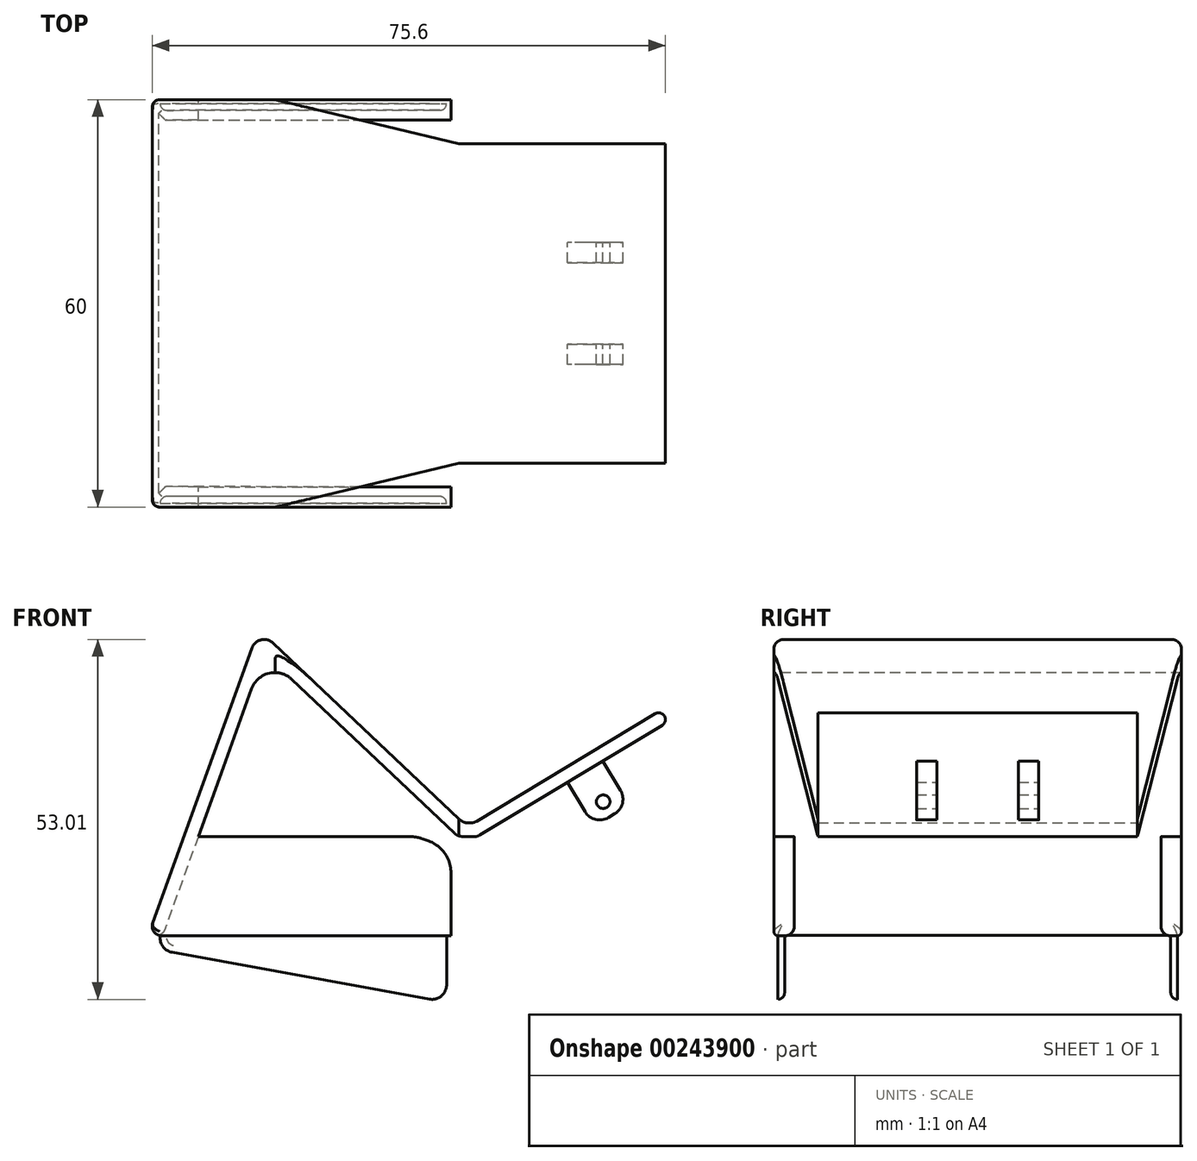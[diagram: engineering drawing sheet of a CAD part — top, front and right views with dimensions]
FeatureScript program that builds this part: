
annotation { "Feature Type Name" : "Feature", "Feature Type Description" : "" }
export const myFeature = defineFeature(function(context is Context, id is Id, definition is map)
    precondition{}
    {
        {
            var Q0;
            Q0=qCreatedBy(makeId("Front.planeOp"),FACE);
            var sketch = newSketch(context, id + "F0", { "sketchPlane" : qUnion([Q0])});
            skPoint(sketch, "E0.middle", {"position": v(-5, 4.31) * mm});
            skLineSegment(sketch, "E1", {"start": v(-52, -14.64) * mm, "end": v(-35.7, 30.54) * mm});
            skLineSegment(sketch, "E2", {"start": v(-35.7, 30.54) * mm, "end": v(-5.57, 2.03) * mm});
            skLineSegment(sketch, "E3", {"start": v(-4.04, 2) * mm, "end": v(-5.57, 2.03) * mm});
            skLineSegment(sketch, "E4", {"start": v(-4.04, 2) * mm, "end": v(23.56, 18.63) * mm});
            skLineSegment(sketch, "E5.0", {"start": v(-3.5, 0) * mm, "end": v(24.59, 16.91) * mm});
            skLineSegment(sketch, "E5.1", {"start": v(-3.5, 0) * mm, "end": v(-6.38, 0.04) * mm});
            skLineSegment(sketch, "E5.2", {"start": v(-34.85, 26.99) * mm, "end": v(-6.38, 0.04) * mm});
            skLineSegment(sketch, "E5.3", {"start": v(-49.86, -14.62) * mm, "end": v(-34.85, 26.99) * mm});
            skLineSegment(sketch, "E6", {"start": v(-49.86, -14.62) * mm, "end": v(-52, -14.64) * mm});
            skLineSegment(sketch, "E7", {"start": v(23.56, 18.63) * mm, "end": v(24.59, 16.91) * mm});
            skSolve(sketch);
        }
        {
            var Q0;
            Q0=makeQuery(id+"F0.imprint","IMPRINT",FACE,{"disambiguationData":[TD([[makeQuery(id+"F0.imprint","IMPRINT",EDGE,{"derivedFrom":sQuery(id+"F0.wireOp",EDGE,"E1")}),-1.0]])]});
            extrude(context, id + "F1", {"entities" : qUnion([Q0]), "endBound" : BoundingType.SYMMETRIC, "depth" : 60 * mm});
        }
        {
            var Q0;
            Q0=makeQuery(id+"F1.opExtrude","SWEPT_EDGE",EDGE,{"disambiguationData":[OSD([sQuery(id+"F0.wireOp",EDGE,"E1"),sQuery(id+"F0.wireOp",EDGE,"E2")])]});
            fillet(context, id + "F2", {"entities" : qUnion([Q0]), "radius" : 1.94 * mm, "tangentPropagation" : true, "allowEdgeOverflow" : false});
        }
        {
            var Q0;
            Q0=makeQuery(id+"F1.opExtrude","SWEPT_EDGE",EDGE,{"disambiguationData":[OSD([sQuery(id+"F0.wireOp",EDGE,"E5.2"),sQuery(id+"F0.wireOp",EDGE,"E5.3")])]});
            fillet(context, id + "F3", {"entities" : qUnion([Q0]), "radius" : 3.63 * mm, "tangentPropagation" : true, "allowEdgeOverflow" : false});
        }
        {
            var Q0;
            Q0=makeQuery(id+"F1.opExtrude","SWEPT_EDGE",EDGE,{"disambiguationData":[OSD([sQuery(id+"F0.wireOp",EDGE,"E5.1"),sQuery(id+"F0.wireOp",EDGE,"E5.2")])]});
            var Q1;
            Q1=makeQuery(id+"F1.opExtrude","SWEPT_EDGE",EDGE,{"disambiguationData":[OSD([sQuery(id+"F0.wireOp",EDGE,"E5.0"),sQuery(id+"F0.wireOp",EDGE,"E5.1")])]});
            var Q2;
            Q2=makeQuery(id+"F1.opExtrude","SWEPT_EDGE",EDGE,{"disambiguationData":[OSD([sQuery(id+"F0.wireOp",EDGE,"E2"),sQuery(id+"F0.wireOp",EDGE,"E3")])]});
            var Q3;
            Q3=makeQuery(id+"F1.opExtrude","SWEPT_EDGE",EDGE,{"disambiguationData":[OSD([sQuery(id+"F0.wireOp",EDGE,"E3"),sQuery(id+"F0.wireOp",EDGE,"E4")])]});
            fillet(context, id + "F4", {"entities" : qUnion([Q0, Q1, Q2, Q3]), "radius" : 1.68 * mm, "allowEdgeOverflow" : false});
        }
        {
            var Q0;
            Q0=makeQuery(id+"F1.opExtrude","SWEPT_FACE",FACE,{"disambiguationData":[OSD([sQuery(id+"F0.wireOp",EDGE,"E5.0")])]});
            var sketch = newSketch(context, id + "F5", { "sketchPlane" : qUnion([Q0])});
            skLineSegment(sketch, "E8.bottom", {"start": v(18.6, 9) * mm, "end": v(12.5, 9) * mm});
            skLineSegment(sketch, "E8.top", {"start": v(18.6, -9) * mm, "end": v(12.5, -9) * mm});
            skLineSegment(sketch, "E8.left", {"start": v(18.6, 9) * mm, "end": v(18.6, -9) * mm});
            skLineSegment(sketch, "E8.right", {"start": v(12.5, 9) * mm, "end": v(12.5, -9) * mm});
            skPoint(sketch, "E8.middle", {"position": v(15.55, 0) * mm});
            skSolve(sketch);
        }
        {
            var Q0;
            Q0=makeQuery(id+"F5.imprint","IMPRINT",FACE,{"disambiguationData":[TD([[makeQuery(id+"F5.imprint","IMPRINT",EDGE,{"derivedFrom":sQuery(id+"F5.wireOp",EDGE,"E8.bottom")}),1.0]])]});
            extrude(context, id + "F6", {"entities" : qUnion([Q0]), "operationType" : NewBodyOperationType.ADD, "depth" : 7.56 * mm});
        }
        {
            var Q0;
            Q0=qCreatedBy(makeId("Front.planeOp"),FACE);
            var sketch = newSketch(context, id + "F7", { "sketchPlane" : qUnion([Q0])});
            skCircle(sketch, "E9", {"center": v(15.05, 5.15) * mm, "radius": 1 * mm});
            skSolve(sketch);
        }
        {
            var Q0;
            Q0 = qSketchRegion(id + "F7", true);
            extrude(context, id + "F8", {"entities" : qUnion([Q0]), "operationType" : NewBodyOperationType.REMOVE, "endBound" : BoundingType.SYMMETRIC, "depth" : 25 * mm});
        }
        {
            var Q0;
            Q0=makeQuery(id+"F1.opExtrude","SWEPT_EDGE",EDGE,{"disambiguationData":[OSD([sQuery(id+"F0.wireOp",EDGE,"E4"),sQuery(id+"F0.wireOp",EDGE,"E7")])]});
            var Q1;
            Q1=makeQuery(id+"F1.opExtrude","SWEPT_EDGE",EDGE,{"disambiguationData":[OSD([sQuery(id+"F0.wireOp",EDGE,"E5.0"),sQuery(id+"F0.wireOp",EDGE,"E7")])]});
            fillet(context, id + "F9", {"entities" : qUnion([Q0, Q1]), "radius" : 1 * mm, "tangentPropagation" : true, "allowEdgeOverflow" : false});
        }
        {
            var Q0;
            Q0=qCreatedBy(makeId("Front.planeOp"),FACE);
            cPlane(context, id + "F10", {"entities" : qUnion([Q0]), "cplaneType" : CPlaneType.OFFSET, "offset" : 21 * mm, "width" : 150 * mm, "height" : 150 * mm});
        }
        {
            var Q0;
            Q0=makeQuery(id+"F1.opExtrude","SWEPT_FACE",FACE,{"disambiguationData":[OSD([sQuery(id+"F0.wireOp",EDGE,"E5.3")])]});
            var sketch = newSketch(context, id + "F11", { "sketchPlane" : qUnion([Q0])});
            skLineSegment(sketch, "E10.0.2", {"start": v(-30, -4.22) * mm, "end": v(-30, -30.67) * mm});
            skLineSegment(sketch, "E10.0.3", {"start": v(-30, -30.67) * mm, "end": v(-27, -30.67) * mm});
            skLineSegment(sketch, "E11", {"start": v(-27.01, -4.28) * mm, "end": v(-27, -30.67) * mm});
            skLineSegment(sketch, "E12", {"start": v(-30, -4.22) * mm, "end": v(-27.01, -4.28) * mm});
            skLineSegment(sketch, "E13.MirrorCS", {"start": v(27.01, -4.28) * mm, "end": v(27, -30.67) * mm});
            skLineSegment(sketch, "E14.MirrorCS", {"start": v(30, -4.22) * mm, "end": v(27.01, -4.28) * mm});
            skLineSegment(sketch, "E15.MirrorCS", {"start": v(30, -4.22) * mm, "end": v(30, -30.67) * mm});
            skLineSegment(sketch, "E16.MirrorCS", {"start": v(30, -30.67) * mm, "end": v(27, -30.67) * mm});
            skSolve(sketch);
        }
        {
            var Q0;
            Q0=makeQuery(id+"F11.imprint","IMPRINT",FACE,{"disambiguationData":[TD([[makeQuery(id+"F11.imprint","IMPRINT",EDGE,{"derivedFrom":sQuery(id+"F11.wireOp",EDGE,"E10.0.2")}),-1.0]])]});
            var Q1;
            Q1=makeQuery(id+"F11.imprint","IMPRINT",FACE,{"disambiguationData":[TD([[makeQuery(id+"F11.imprint","IMPRINT",EDGE,{"derivedFrom":sQuery(id+"F11.wireOp",EDGE,"E13.MirrorCS")}),1.0]])]});
            extrude(context, id + "F12", {"entities" : qUnion([Q0, Q1]), "operationType" : NewBodyOperationType.ADD, "depth" : 76.5 * mm});
        }
        {
            var Q0;
            Q0=qCreatedBy(makeId("Top.planeOp"),FACE);
            var sketch = newSketch(context, id + "F13", { "sketchPlane" : qUnion([Q0])});
            skLineSegment(sketch, "E17", {"start": v(36.3, -23.5) * mm, "end": v(-6.2, -23.5) * mm});
            skLineSegment(sketch, "E18", {"start": v(0, -31.57) * mm, "end": v(36.72, -31.57) * mm});
            skLineSegment(sketch, "E19", {"start": v(36.72, -31.57) * mm, "end": v(36.3, -23.5) * mm});
            skLineSegment(sketch, "E20", {"start": v(-6.2, -23.5) * mm, "end": v(-33.5, -30.06) * mm});
            skLineSegment(sketch, "E21", {"start": v(0, -31.57) * mm, "end": v(-39.78, -31.57) * mm});
            skLineSegment(sketch, "E22", {"start": v(-33.5, -30.06) * mm, "end": v(-39.78, -31.57) * mm});
            skLineSegment(sketch, "E23.MirrorCS", {"start": v(36.3, 23.5) * mm, "end": v(-6.2, 23.5) * mm});
            skLineSegment(sketch, "E24.MirrorCS", {"start": v(-6.2, 23.5) * mm, "end": v(-33.5, 30.06) * mm});
            skLineSegment(sketch, "E25.MirrorCS", {"start": v(-33.5, 30.06) * mm, "end": v(-39.78, 31.57) * mm});
            skLineSegment(sketch, "E26.MirrorCS", {"start": v(0, 31.57) * mm, "end": v(-39.78, 31.57) * mm});
            skLineSegment(sketch, "E27.MirrorCS", {"start": v(0, 31.57) * mm, "end": v(36.72, 31.57) * mm});
            skLineSegment(sketch, "E28.MirrorCS", {"start": v(36.72, 31.57) * mm, "end": v(36.3, 23.5) * mm});
            skSolve(sketch);
        }
        {
            var Q0;
            Q0=makeQuery(id+"F13.imprint","IMPRINT",FACE,{"disambiguationData":[TD([[makeQuery(id+"F13.imprint","IMPRINT",EDGE,{"derivedFrom":sQuery(id+"F13.wireOp",EDGE,"E17")}),1.0]])]});
            var Q1;
            Q1=makeQuery(id+"F13.imprint","IMPRINT",FACE,{"disambiguationData":[TD([[makeQuery(id+"F13.imprint","IMPRINT",EDGE,{"derivedFrom":sQuery(id+"F13.wireOp",EDGE,"E24.MirrorCS")}),-1.0]])]});
            extrude(context, id + "F14", {"entities" : qUnion([Q0, Q1]), "operationType" : NewBodyOperationType.REMOVE, "depth" : 103.2 * mm});
        }
        {
            var Q0;
            Q0=qCreatedBy(id+"F10.planeOp",FACE);
            var sketch = newSketch(context, id + "F15", { "sketchPlane" : qUnion([Q0])});
            skLineSegment(sketch, "E29.top", {"start": v(-52.62, -40.85) * mm, "end": v(33.9, -40.85) * mm});
            skLineSegment(sketch, "E29.left", {"start": v(-52.62, -14.6) * mm, "end": v(-52.62, -40.85) * mm});
            skLineSegment(sketch, "E29.right", {"start": v(33.9, -14.6) * mm, "end": v(33.9, -40.85) * mm});
            skLineSegment(sketch, "E30", {"start": v(-52.62, -14.6) * mm, "end": v(-7.36, -14.6) * mm});
            skLineSegment(sketch, "E31", {"start": v(-7.36, -14.6) * mm, "end": v(-7.36, -0.89) * mm});
            skLineSegment(sketch, "E32", {"start": v(-7.36, -0.89) * mm, "end": v(34.02, -0.89) * mm});
            skLineSegment(sketch, "E33", {"start": v(34.02, -0.89) * mm, "end": v(33.9, -14.6) * mm});
            skSolve(sketch);
        }
        {
            var Q0;
            Q0=makeQuery(id+"F15.imprint","IMPRINT",FACE,{"disambiguationData":[TD([[makeQuery(id+"F15.imprint","IMPRINT",EDGE,{"derivedFrom":sQuery(id+"F15.wireOp",EDGE,"E29.top")}),1.0]])]});
            extrude(context, id + "F16", {"entities" : qUnion([Q0]), "operationType" : NewBodyOperationType.REMOVE, "endBound" : BoundingType.SYMMETRIC, "oppositeDirection" : true, "depth" : 138.8 * mm});
        }
        {
            var Q0;
            Q0=qCreatedBy(id+"F10.planeOp",FACE);
            var sketch = newSketch(context, id + "F17", { "sketchPlane" : qUnion([Q0])});
            skLineSegment(sketch, "E34", {"start": v(-11.2, 0) * mm, "end": v(-44.59, 0) * mm});
            skLineSegment(sketch, "E35", {"start": v(-44.59, 0) * mm, "end": v(-40.5, 11.36) * mm});
            skLineSegment(sketch, "E36", {"start": v(-40.5, 11.36) * mm, "end": v(-11.2, 0) * mm});
            skSolve(sketch);
        }
        {
            var Q0;
            Q0=makeQuery(id+"F17.imprint","IMPRINT",FACE,{"disambiguationData":[TD([[makeQuery(id+"F17.imprint","IMPRINT",EDGE,{"derivedFrom":sQuery(id+"F17.wireOp",EDGE,"E34")}),-1.0]])]});
            extrude(context, id + "F18", {"entities" : qUnion([Q0]), "operationType" : NewBodyOperationType.REMOVE, "endBound" : BoundingType.SYMMETRIC, "depth" : 138.2 * mm});
        }
        {
            var Q0;
            {var subQ0=sQuery(id+"F11.wireOp",EDGE,"E11");var subQ1=sQuery(id+"F11.wireOp",EDGE,"E12");var subQ2=sQuery(id+"F11.wireOp",EDGE,"E10.0.2");Q0=makeQuery(id+"F16.boolean.opBoolean","INTERSECT",EDGE,{"derivedFrom":[makeQuery(id+"F14.boolean.opBoolean","SPLIT",FACE,{"disambiguationData":[TD([makeQuery(id+"F12.opExtrude","CAP_FACE",FACE,{"disambiguationData":[OSD([subQ2,sQuery(id+"F11.wireOp",EDGE,"E10.0.3"),subQ0,subQ1])],"isStart":false})])],"derivedFrom":makeQuery(id+"F12.opExtrude","SWEPT_FACE",FACE,{"disambiguationData":[OSD([subQ1])]})}),makeQuery(id+"F16.opExtrude","SWEPT_FACE",FACE,{"disambiguationData":[OSD([sQuery(id+"F15.wireOp",EDGE,"E31")])]})]});}
            var Q1;
            Q1=makeQuery(id+"F14.boolean.opBoolean","INTERSECT",EDGE,{"derivedFrom":[makeQuery(id+"F12.opExtrude","SWEPT_FACE",FACE,{"disambiguationData":[OSD([sQuery(id+"F11.wireOp",EDGE,"E12")])]}),makeQuery(id+"F14.opExtrude","CAP_FACE",FACE,{"disambiguationData":[OSD([sQuery(id+"F13.wireOp",EDGE,"E17"),sQuery(id+"F13.wireOp",EDGE,"E18"),sQuery(id+"F13.wireOp",EDGE,"E19"),sQuery(id+"F13.wireOp",EDGE,"E20"),sQuery(id+"F13.wireOp",EDGE,"E21"),sQuery(id+"F13.wireOp",EDGE,"E22")])],"isStart":true})]});
            var Q2;
            {var subQ0=sQuery(id+"F11.wireOp",EDGE,"E15.MirrorCS");var subQ1=sQuery(id+"F11.wireOp",EDGE,"E14.MirrorCS");var subQ2=sQuery(id+"F11.wireOp",EDGE,"E13.MirrorCS");Q2=makeQuery(id+"F16.boolean.opBoolean","INTERSECT",EDGE,{"derivedFrom":[makeQuery(id+"F14.boolean.opBoolean","SPLIT",FACE,{"disambiguationData":[TD([makeQuery(id+"F12.opExtrude","CAP_FACE",FACE,{"disambiguationData":[OSD([subQ2,subQ1,subQ0,sQuery(id+"F11.wireOp",EDGE,"E16.MirrorCS")])],"isStart":false})])],"derivedFrom":makeQuery(id+"F12.opExtrude","SWEPT_FACE",FACE,{"disambiguationData":[OSD([subQ1])]})}),makeQuery(id+"F16.opExtrude","SWEPT_FACE",FACE,{"disambiguationData":[OSD([sQuery(id+"F15.wireOp",EDGE,"E31")])]})]});}
            var Q3;
            Q3=makeQuery(id+"F14.boolean.opBoolean","INTERSECT",EDGE,{"derivedFrom":[makeQuery(id+"F12.opExtrude","SWEPT_FACE",FACE,{"disambiguationData":[OSD([sQuery(id+"F11.wireOp",EDGE,"E14.MirrorCS")])]}),makeQuery(id+"F14.opExtrude","CAP_FACE",FACE,{"disambiguationData":[OSD([sQuery(id+"F13.wireOp",EDGE,"E24.MirrorCS"),sQuery(id+"F13.wireOp",EDGE,"E25.MirrorCS"),sQuery(id+"F13.wireOp",EDGE,"E26.MirrorCS"),sQuery(id+"F13.wireOp",EDGE,"E27.MirrorCS"),sQuery(id+"F13.wireOp",EDGE,"E28.MirrorCS"),sQuery(id+"F13.wireOp",EDGE,"E23.MirrorCS")])],"isStart":true})]});
            fillet(context, id + "F19", {"entities" : qUnion([Q0, Q1, Q2, Q3]), "radius" : 5 * mm, "tangentPropagation" : true, "allowEdgeOverflow" : false});
        }
        {
            var Q0;
            Q0=qCreatedBy(makeId("Top.planeOp"),FACE);
            cPlane(context, id + "F20", {"entities" : qUnion([Q0]), "cplaneType" : CPlaneType.OFFSET, "offset" : 14.6 * mm, "oppositeDirection" : true, "width" : 150 * mm, "height" : 150 * mm});
        }
        {
            var Q0;
            Q0=qCreatedBy(id+"F20.planeOp",FACE);
            var sketch = newSketch(context, id + "F21", { "sketchPlane" : qUnion([Q0])});
            skLineSegment(sketch, "E37.0.0", {"start": v(-8.02, 28.44) * mm, "end": v(-50.21, 28.43) * mm});
            skLineSegment(sketch, "E37.0.1", {"start": v(-50.21, 28.43) * mm, "end": v(-50.21, 29.43) * mm});
            skLineSegment(sketch, "E37.0.2", {"start": v(-50.21, 29.43) * mm, "end": v(-8.02, 29.43) * mm});
            skLineSegment(sketch, "E37.0.3", {"start": v(-8.02, 29.43) * mm, "end": v(-8.02, 28.44) * mm});
            skLineSegment(sketch, "E38.MirrorCS", {"start": v(-50.21, -29.43) * mm, "end": v(-8.02, -29.43) * mm});
            skLineSegment(sketch, "E39.MirrorCS", {"start": v(-8.02, -28.44) * mm, "end": v(-50.21, -28.43) * mm});
            skLineSegment(sketch, "E40.MirrorCS", {"start": v(-50.21, -28.43) * mm, "end": v(-50.21, -29.43) * mm});
            skLineSegment(sketch, "E41.MirrorCS", {"start": v(-8.02, -29.43) * mm, "end": v(-8.02, -28.44) * mm});
            skSolve(sketch);
        }
        {
            var Q0;
            Q0=makeQuery(id+"F21.imprint","IMPRINT",FACE,{"disambiguationData":[TD([[makeQuery(id+"F21.imprint","IMPRINT",EDGE,{"derivedFrom":sQuery(id+"F21.wireOp",EDGE,"E37.0.0")}),-1.0]])]});
            var Q1;
            Q1=makeQuery(id+"F21.imprint","IMPRINT",FACE,{"disambiguationData":[TD([[makeQuery(id+"F21.imprint","IMPRINT",EDGE,{"derivedFrom":sQuery(id+"F21.wireOp",EDGE,"E38.MirrorCS")}),1.0]])]});
            extrude(context, id + "F22", {"entities" : qUnion([Q0, Q1]), "oppositeDirection" : true, "depth" : 9.8 * mm});
        }
        {
            var Q0;
            Q0=qCreatedBy(makeId("Front.planeOp"),FACE);
            var sketch = newSketch(context, id + "F23", { "sketchPlane" : qUnion([Q0])});
            skLineSegment(sketch, "E42", {"start": v(-53.01, -16.2) * mm, "end": v(-6.88, -24.6) * mm});
            skLineSegment(sketch, "E43", {"start": v(-6.88, -24.6) * mm, "end": v(-53.38, -24.6) * mm});
            skLineSegment(sketch, "E44", {"start": v(-53.38, -24.6) * mm, "end": v(-53.01, -16.2) * mm});
            skSolve(sketch);
        }
        {
            var Q0;
            Q0=makeQuery(id+"F23.imprint","IMPRINT",FACE,{"disambiguationData":[TD([[makeQuery(id+"F23.imprint","IMPRINT",EDGE,{"derivedFrom":sQuery(id+"F23.wireOp",EDGE,"E42")}),-1.0]])]});
            extrude(context, id + "F24", {"entities" : qUnion([Q0]), "operationType" : NewBodyOperationType.REMOVE, "endBound" : BoundingType.SYMMETRIC, "depth" : 66.2 * mm});
        }
        {
            var Q0;
            {var subQ0=sQuery(id+"F0.wireOp",EDGE,"E2");var subQ1=sQuery(id+"F0.wireOp",EDGE,"E1");var subQ4=sQuery(id+"F11.wireOp",EDGE,"E10.0.2");var subQ7=sQuery(id+"F0.wireOp",EDGE,"E6");var subQ8=sQuery(id+"F0.wireOp",EDGE,"E5.3");var subQ9=sQuery(id+"F0.wireOp",EDGE,"E5.2");Q0=makeQuery(id+"F16.boolean.opBoolean","INTERSECT",EDGE,{"derivedFrom":[makeQuery(id+"F14.boolean.opBoolean","SPLIT",FACE,{"disambiguationData":[TD([makeQuery(id+"F1.opExtrude","SWEPT_FACE",FACE,{"disambiguationData":[OSD([subQ1])]})])],"derivedFrom":makeQuery(id+"F12.boolean.opBoolean","MERGE",FACE,{"derivedFrom":[makeQuery(id+"F1.opExtrude","CAP_FACE",FACE,{"disambiguationData":[OSD([subQ1,subQ0,sQuery(id+"F0.wireOp",EDGE,"E3"),sQuery(id+"F0.wireOp",EDGE,"E4"),sQuery(id+"F0.wireOp",EDGE,"E5.0"),sQuery(id+"F0.wireOp",EDGE,"E5.1"),subQ9,subQ8,subQ7,sQuery(id+"F0.wireOp",EDGE,"E7")])],"isStart":false}),makeQuery(id+"F12.opExtrude","SWEPT_FACE",FACE,{"disambiguationData":[OSD([subQ4])]})]})}),makeQuery(id+"F16.opExtrude","SWEPT_FACE",FACE,{"disambiguationData":[OSD([sQuery(id+"F15.wireOp",EDGE,"E30")])]})]});}
            var Q1;
            {var subQ0=sQuery(id+"F0.wireOp",EDGE,"E2");var subQ1=sQuery(id+"F0.wireOp",EDGE,"E1");var subQ2=sQuery(id+"F0.wireOp",EDGE,"E6");var subQ4=sQuery(id+"F0.wireOp",EDGE,"E5.3");var subQ5=sQuery(id+"F11.wireOp",EDGE,"E15.MirrorCS");var subQ7=sQuery(id+"F0.wireOp",EDGE,"E5.2");Q1=makeQuery(id+"F16.boolean.opBoolean","INTERSECT",EDGE,{"derivedFrom":[makeQuery(id+"F14.boolean.opBoolean","SPLIT",FACE,{"disambiguationData":[TD([makeQuery(id+"F1.opExtrude","SWEPT_FACE",FACE,{"disambiguationData":[OSD([subQ1])]})])],"derivedFrom":makeQuery(id+"F12.boolean.opBoolean","MERGE",FACE,{"derivedFrom":[makeQuery(id+"F1.opExtrude","CAP_FACE",FACE,{"disambiguationData":[OSD([subQ1,subQ0,sQuery(id+"F0.wireOp",EDGE,"E3"),sQuery(id+"F0.wireOp",EDGE,"E4"),sQuery(id+"F0.wireOp",EDGE,"E5.0"),sQuery(id+"F0.wireOp",EDGE,"E5.1"),subQ7,subQ4,subQ2,sQuery(id+"F0.wireOp",EDGE,"E7")])],"isStart":true}),makeQuery(id+"F12.opExtrude","SWEPT_FACE",FACE,{"disambiguationData":[OSD([subQ5])]})]})}),makeQuery(id+"F16.opExtrude","SWEPT_FACE",FACE,{"disambiguationData":[OSD([sQuery(id+"F15.wireOp",EDGE,"E30")])]})]});}
            fillet(context, id + "F25", {"entities" : qUnion([Q0, Q1]), "radius" : 0.6 * mm, "tangentPropagation" : true, "allowEdgeOverflow" : false});
        }
        {
            var Q0;
            Q0=makeQuery(id+"F24.boolean.opBoolean","INTERSECT",EDGE,{"derivedFrom":[makeQuery(id+"F22.opExtrude","SWEPT_FACE",FACE,{"disambiguationData":[OSD([sQuery(id+"F21.wireOp",EDGE,"E40.MirrorCS")])]}),makeQuery(id+"F24.opExtrude","SWEPT_FACE",FACE,{"disambiguationData":[OSD([sQuery(id+"F23.wireOp",EDGE,"E42")])]})]});
            var Q1;
            Q1=makeQuery(id+"F24.boolean.opBoolean","INTERSECT",EDGE,{"derivedFrom":[makeQuery(id+"F22.opExtrude","SWEPT_FACE",FACE,{"disambiguationData":[OSD([sQuery(id+"F21.wireOp",EDGE,"E37.0.1")])]}),makeQuery(id+"F24.opExtrude","SWEPT_FACE",FACE,{"disambiguationData":[OSD([sQuery(id+"F23.wireOp",EDGE,"E42")])]})]});
            var Q2;
            Q2=makeQuery(id+"F24.boolean.opBoolean","INTERSECT",EDGE,{"derivedFrom":[makeQuery(id+"F22.opExtrude","SWEPT_FACE",FACE,{"disambiguationData":[OSD([sQuery(id+"F21.wireOp",EDGE,"E41.MirrorCS")])]}),makeQuery(id+"F24.opExtrude","SWEPT_FACE",FACE,{"disambiguationData":[OSD([sQuery(id+"F23.wireOp",EDGE,"E42")])]})]});
            var Q3;
            Q3=makeQuery(id+"F24.boolean.opBoolean","INTERSECT",EDGE,{"derivedFrom":[makeQuery(id+"F22.opExtrude","SWEPT_FACE",FACE,{"disambiguationData":[OSD([sQuery(id+"F21.wireOp",EDGE,"E37.0.3")])]}),makeQuery(id+"F24.opExtrude","SWEPT_FACE",FACE,{"disambiguationData":[OSD([sQuery(id+"F23.wireOp",EDGE,"E42")])]})]});
            fillet(context, id + "F26", {"entities" : qUnion([Q0, Q1, Q2, Q3]), "radius" : 2.13 * mm, "tangentPropagation" : true, "allowEdgeOverflow" : false});
        }
        {
            var Q0;
            Q0=makeQuery(id+"F24.boolean.opBoolean","INTERSECT",EDGE,{"derivedFrom":[makeQuery(id+"F22.opExtrude","SWEPT_FACE",FACE,{"disambiguationData":[OSD([sQuery(id+"F21.wireOp",EDGE,"E39.MirrorCS")])]}),makeQuery(id+"F24.opExtrude","SWEPT_FACE",FACE,{"disambiguationData":[OSD([sQuery(id+"F23.wireOp",EDGE,"E42")])]})]});
            var Q1;
            Q1=makeQuery(id+"F24.boolean.opBoolean","INTERSECT",EDGE,{"derivedFrom":[makeQuery(id+"F22.opExtrude","SWEPT_FACE",FACE,{"disambiguationData":[OSD([sQuery(id+"F21.wireOp",EDGE,"E37.0.0")])]}),makeQuery(id+"F24.opExtrude","SWEPT_FACE",FACE,{"disambiguationData":[OSD([sQuery(id+"F23.wireOp",EDGE,"E42")])]})]});
            fillet(context, id + "F27", {"entities" : qUnion([Q0, Q1]), "radius" : 1 * mm, "tangentPropagation" : true, "allowEdgeOverflow" : false});
        }
        {
            var Q0;
            Q0=makeQuery(id+"F16.boolean.opBoolean","INTERSECT",EDGE,{"derivedFrom":[makeQuery(id+"F12.opExtrude","SWEPT_FACE",FACE,{"disambiguationData":[OSD([sQuery(id+"F11.wireOp",EDGE,"E11")])]}),makeQuery(id+"F16.opExtrude","SWEPT_FACE",FACE,{"disambiguationData":[OSD([sQuery(id+"F15.wireOp",EDGE,"E30")])]})]});
            var Q1;
            Q1=makeQuery(id+"F16.boolean.opBoolean","INTERSECT",EDGE,{"derivedFrom":[makeQuery(id+"F12.opExtrude","SWEPT_FACE",FACE,{"disambiguationData":[OSD([sQuery(id+"F11.wireOp",EDGE,"E13.MirrorCS")])]}),makeQuery(id+"F16.opExtrude","SWEPT_FACE",FACE,{"disambiguationData":[OSD([sQuery(id+"F15.wireOp",EDGE,"E30")])]})]});
            var Q2;
            Q2=makeQuery(id+"F16.boolean.opBoolean","INTERSECT",EDGE,{"derivedFrom":[makeQuery(id+"F1.opExtrude","SWEPT_FACE",FACE,{"disambiguationData":[OSD([sQuery(id+"F0.wireOp",EDGE,"E5.3")])]}),makeQuery(id+"F16.opExtrude","SWEPT_FACE",FACE,{"disambiguationData":[OSD([sQuery(id+"F15.wireOp",EDGE,"E30")])]})]});
            var Q3;
            Q3=makeQuery(id+"F16.boolean.opBoolean","INTERSECT",EDGE,{"derivedFrom":[makeQuery(id+"F1.opExtrude","SWEPT_FACE",FACE,{"disambiguationData":[OSD([sQuery(id+"F0.wireOp",EDGE,"E1")])]}),makeQuery(id+"F16.opExtrude","SWEPT_FACE",FACE,{"disambiguationData":[OSD([sQuery(id+"F15.wireOp",EDGE,"E30")])]})]});
            fillet(context, id + "F28", {"entities" : qUnion([Q0, Q1, Q2, Q3]), "radius" : 1.4 * mm, "tangentPropagation" : true, "allowEdgeOverflow" : false});
        }
        {
            var Q0;
            Q0=makeQuery(id+"F6.opExtrude","SWEPT_FACE",FACE,{"disambiguationData":[OSD([sQuery(id+"F5.wireOp",EDGE,"E8.left")])]});
            var sketch = newSketch(context, id + "F29", { "sketchPlane" : qUnion([Q0])});
            skLineSegment(sketch, "E45.bottom", {"start": v(-6, -5.76) * mm, "end": v(6, -5.76) * mm});
            skLineSegment(sketch, "E45.top", {"start": v(-6, 1.8) * mm, "end": v(6, 1.8) * mm});
            skLineSegment(sketch, "E45.left", {"start": v(-6, -5.76) * mm, "end": v(-6, 1.8) * mm});
            skLineSegment(sketch, "E45.right", {"start": v(6, -5.76) * mm, "end": v(6, 1.8) * mm});
            skPoint(sketch, "E45.middle", {"position": v(0, -1.98) * mm});
            skSolve(sketch);
        }
        {
            var Q0;
            {var subQ0=sQuery(id+"F29.wireOp",EDGE,"3f86a7f2-364d-43cf-a6ba-87053ab2ad43.0.0");Q0=makeQuery(id+"F29.imprint","IMPRINT",FACE,{"disambiguationData":[TD([[makeQuery(id+"F29.imprint","IMPRINT",EDGE,{"derivedFrom":subQ0}),1.0]])]});}
            var Q1;
            Q1=makeQuery(id+"F29.imprint","IMPRINT",FACE,{"disambiguationData":[TD([[makeQuery(id+"F29.imprint","IMPRINT",EDGE,{"derivedFrom":sQuery(id+"F29.wireOp",EDGE,"E45.bottom")}),1.0]])]});
            extrude(context, id + "F30", {"entities" : qUnion([Q0, Q1]), "operationType" : NewBodyOperationType.REMOVE, "endBound" : BoundingType.SYMMETRIC, "depth" : 25 * mm});
        }
        {
            var Q0;
            {var subQ0=sQuery(id+"F5.wireOp",EDGE,"E8.left");var subQ1=sQuery(id+"F5.wireOp",EDGE,"E8.top");Q0=makeQuery(id+"F30.boolean.opBoolean","SPLIT",EDGE,{"disambiguationData":[TD([makeQuery(id+"F6.opExtrude","SWEPT_FACE",FACE,{"disambiguationData":[OSD([subQ1])]})])],"derivedFrom":makeQuery(id+"F6.opExtrude","CAP_EDGE",EDGE,{"disambiguationData":[OSD([subQ0])],"isStart":false})});}
            var Q1;
            {var subQ0=sQuery(id+"F5.wireOp",EDGE,"E8.bottom");var subQ1=sQuery(id+"F5.wireOp",EDGE,"E8.left");Q1=makeQuery(id+"F30.boolean.opBoolean","SPLIT",EDGE,{"disambiguationData":[TD([makeQuery(id+"F6.opExtrude","SWEPT_FACE",FACE,{"disambiguationData":[OSD([subQ0])]})])],"derivedFrom":makeQuery(id+"F6.opExtrude","CAP_EDGE",EDGE,{"disambiguationData":[OSD([subQ1])],"isStart":false})});}
            var Q2;
            {var subQ0=sQuery(id+"F5.wireOp",EDGE,"E8.right");var subQ1=sQuery(id+"F5.wireOp",EDGE,"E8.top");Q2=makeQuery(id+"F30.boolean.opBoolean","SPLIT",EDGE,{"disambiguationData":[TD([makeQuery(id+"F6.opExtrude","SWEPT_FACE",FACE,{"disambiguationData":[OSD([subQ1])]})])],"derivedFrom":makeQuery(id+"F6.opExtrude","CAP_EDGE",EDGE,{"disambiguationData":[OSD([subQ0])],"isStart":false})});}
            var Q3;
            {var subQ0=sQuery(id+"F5.wireOp",EDGE,"E8.bottom");var subQ1=sQuery(id+"F5.wireOp",EDGE,"E8.right");Q3=makeQuery(id+"F30.boolean.opBoolean","SPLIT",EDGE,{"disambiguationData":[TD([makeQuery(id+"F6.opExtrude","SWEPT_FACE",FACE,{"disambiguationData":[OSD([subQ0])]})])],"derivedFrom":makeQuery(id+"F6.opExtrude","CAP_EDGE",EDGE,{"disambiguationData":[OSD([subQ1])],"isStart":false})});}
            fillet(context, id + "F31", {"entities" : qUnion([Q0, Q1, Q2, Q3]), "radius" : 2.53 * mm, "tangentPropagation" : true, "allowEdgeOverflow" : false});
        }
    });
